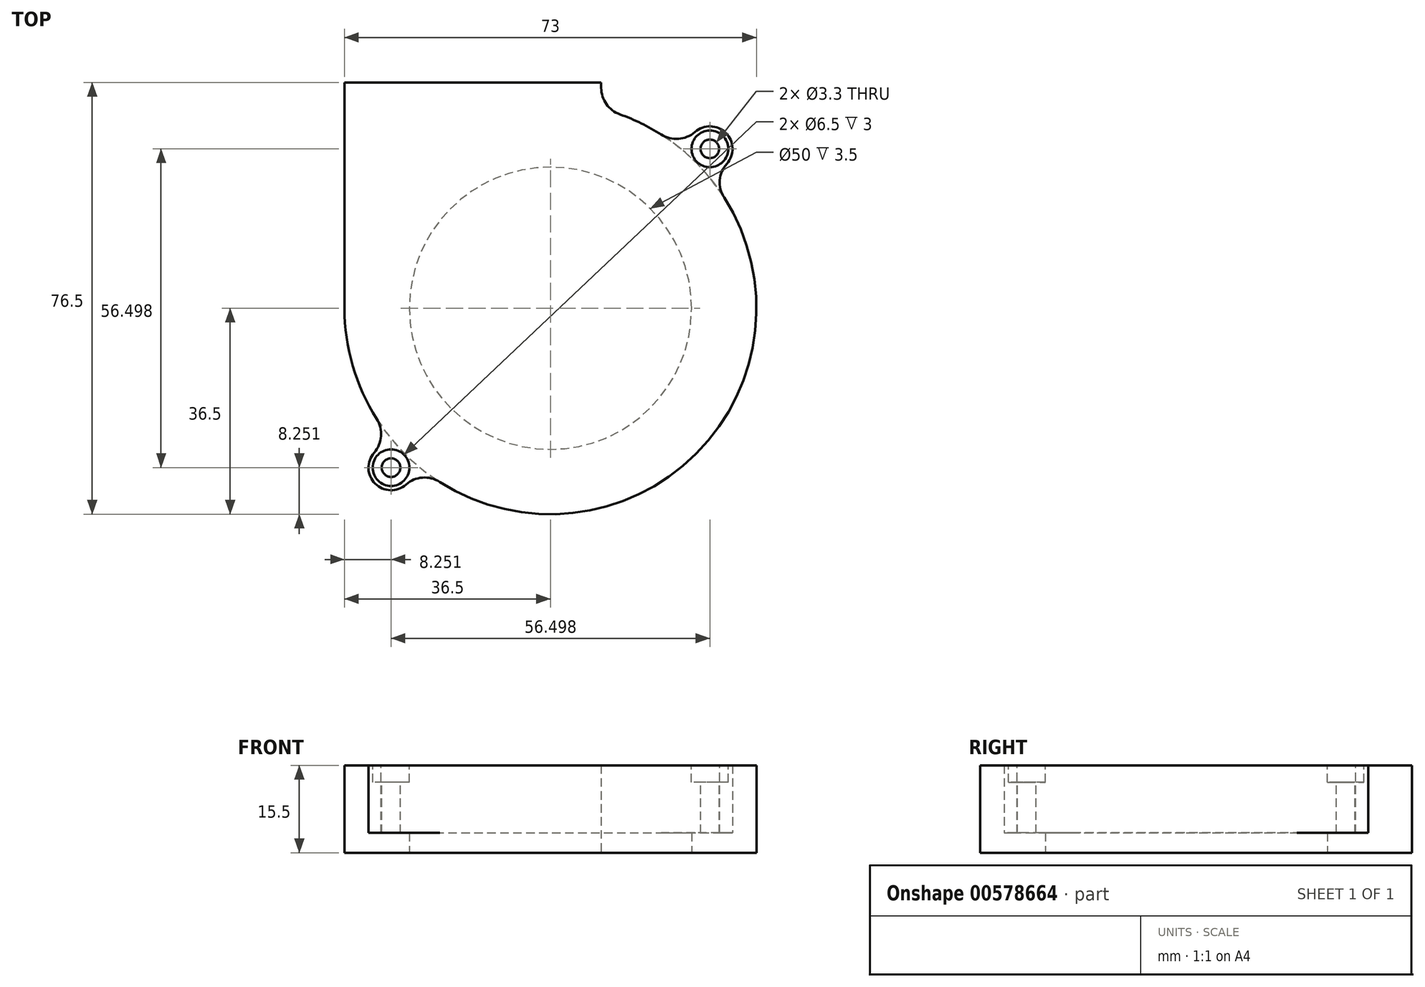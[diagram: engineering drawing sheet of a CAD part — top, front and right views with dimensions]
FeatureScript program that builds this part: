
annotation { "Feature Type Name" : "Feature", "Feature Type Description" : "" }
export const myFeature = defineFeature(function(context is Context, id is Id, definition is map)
    precondition{}
    {
        {
            var Q0;
            Q0=qCreatedBy(makeId("Top.planeOp"),FACE);
            var sketch = newSketch(context, id + "F0", { "sketchPlane" : qUnion([Q0])});
            skArc(sketch, "E0", {"start": v(24.4, 27.14) * mm, "mid": v(17.2, 32.2) * mm, "end": v(9, 35.37) * mm});
            skLineSegment(sketch, "E1", {"start": v(9, 40) * mm, "end": v(-36.5, 40) * mm});
            skLineSegment(sketch, "E2", {"start": v(-36.5, 40) * mm, "end": v(-36.5, 0) * mm});
            skLineSegment(sketch, "E3", {"start": v(9, 40) * mm, "end": v(9, 35.37) * mm});
            skArc(sketch, "E4", {"start": v(27.14, 24.4) * mm, "mid": v(31.08, 31.08) * mm, "end": v(24.4, 27.14) * mm});
            skArc(sketch, "E5", {"start": v(-27.14, -24.4) * mm, "mid": v(-31.08, -31.08) * mm, "end": v(-24.4, -27.14) * mm});
            skLineSegment(sketch, "E6", {"start": v(28.25, 28.25) * mm, "end": v(-28.25, -28.25) * mm, "construction": true});
            skArc(sketch, "E7.trimOffspring", {"start": v(-24.4, -27.14) * mm, "mid": v(25.8, -25.8) * mm, "end": v(27.14, 24.4) * mm});
            skArc(sketch, "E8.trimOffspring", {"start": v(-36.5, 0) * mm, "mid": v(-34.08, -13.07) * mm, "end": v(-27.14, -24.4) * mm});
            skSolve(sketch);
        }
        {
            var Q0;
            Q0 = qSketchRegion(id + "F0", true);
            extrude(context, id + "F1", {"entities" : qUnion([Q0]), "depth" : 15.5 * mm, "offsetDistance" : 25 * mm});
        }
        {
            var Q0;
            Q0=makeQuery(id+"F1.opExtrude","CAP_FACE",FACE,{"disambiguationData":[OSD([sQuery(id+"F0.wireOp",EDGE,"E0"),sQuery(id+"F0.wireOp",EDGE,"E1"),sQuery(id+"F0.wireOp",EDGE,"E2"),sQuery(id+"F0.wireOp",EDGE,"E3"),sQuery(id+"F0.wireOp",EDGE,"E4"),sQuery(id+"F0.wireOp",EDGE,"E5"),sQuery(id+"F0.wireOp",EDGE,"E7.trimOffspring"),sQuery(id+"F0.wireOp",EDGE,"E8.trimOffspring")])],"isStart":true});
            var sketch = newSketch(context, id + "F2", { "sketchPlane" : qUnion([Q0])});
            skArc(sketch, "E9", {"start": v(24.4, -27.14) * mm, "mid": v(25.8, -25.8) * mm, "end": v(27.14, -24.4) * mm});
            skArc(sketch, "E10.0", {"start": v(-27.14, 24.4) * mm, "mid": v(-31.08, 31.08) * mm, "end": v(-24.4, 27.14) * mm});
            skArc(sketch, "E11.0", {"start": v(27.14, -24.4) * mm, "mid": v(31.08, -31.08) * mm, "end": v(24.4, -27.14) * mm});
            skArc(sketch, "E12.trimOffspring", {"start": v(-24.4, 27.14) * mm, "mid": v(-25.8, 25.8) * mm, "end": v(-27.14, 24.4) * mm});
            skCircle(sketch, "E13", {"center": v(0, 0) * mm, "radius": 25 * mm});
            skSolve(sketch);
        }
        {
            var Q0;
            Q0=makeQuery(id+"F2.imprint","IMPRINT",FACE,{"disambiguationData":[TD([[makeQuery(id+"F2.imprint","IMPRINT",EDGE,{"derivedFrom":sQuery(id+"F2.wireOp",EDGE,"E10.0")}),-1.0]])]});
            var Q1;
            Q1=makeQuery(id+"F2.imprint","IMPRINT",FACE,{"disambiguationData":[TD([[makeQuery(id+"F2.imprint","IMPRINT",EDGE,{"derivedFrom":sQuery(id+"F2.wireOp",EDGE,"E9")}),-1.0]])]});
            var Q2;
            Q2=makeQuery(id+"F2.imprint","IMPRINT",FACE,{"disambiguationData":[TD([[makeQuery(id+"F2.imprint","IMPRINT",EDGE,{"derivedFrom":sQuery(id+"F2.wireOp",EDGE,"E13")}),1.0]])]});
            extrude(context, id + "F3", {"entities" : qUnion([Q0, Q1, Q2]), "operationType" : NewBodyOperationType.REMOVE, "oppositeDirection" : true, "depth" : 3.5 * mm, "offsetDistance" : 25 * mm});
        }
        {
            var Q0;
            Q0=makeQuery(id+"F1.opExtrude","CAP_FACE",FACE,{"disambiguationData":[OSD([sQuery(id+"F0.wireOp",EDGE,"E0"),sQuery(id+"F0.wireOp",EDGE,"E1"),sQuery(id+"F0.wireOp",EDGE,"E2"),sQuery(id+"F0.wireOp",EDGE,"E3"),sQuery(id+"F0.wireOp",EDGE,"E4"),sQuery(id+"F0.wireOp",EDGE,"E5"),sQuery(id+"F0.wireOp",EDGE,"E7.trimOffspring"),sQuery(id+"F0.wireOp",EDGE,"E8.trimOffspring")])],"isStart":false});
            var sketch = newSketch(context, id + "F4", { "sketchPlane" : qUnion([Q0])});
            skPoint(sketch, "E14", {"position": v(-28.25, -28.25) * mm});
            skPoint(sketch, "E15", {"position": v(28.25, 28.25) * mm});
            skSolve(sketch);
        }
        {
            var Q0;
            Q0=sQuery(id+"F4.wireOp",VERTEX,"E14");
            var Q1;
            Q1=sQuery(id+"F4.wireOp",VERTEX,"E15");
            var Q2;
            Q2=makeQuery(id+"F1.opExtrude","SWEPT_BODY",BODY,{"disambiguationData":[OSD([sQuery(id+"F0.wireOp",EDGE,"E0"),sQuery(id+"F0.wireOp",EDGE,"E1"),sQuery(id+"F0.wireOp",EDGE,"E2"),sQuery(id+"F0.wireOp",EDGE,"E3"),sQuery(id+"F0.wireOp",EDGE,"E4"),sQuery(id+"F0.wireOp",EDGE,"E5"),sQuery(id+"F0.wireOp",EDGE,"E7.trimOffspring"),sQuery(id+"F0.wireOp",EDGE,"E8.trimOffspring")])]});
            hole(context, id + "F5", {"style" : HoleStyle.C_BORE, "endStyle" : HoleEndStyle.THROUGH, "standardTappedOrClearance" : lookupTablePath({ "standard" : "ISO", "fit" : "Normal", "size" : "M3", "type" : "Clearance" }), "standardBlindInLast" : lookupTablePath({ "fit" : "Standard", "standard" : "ISO", "size" : "M3", "type" : "Clearance" }), "holeDiameter" : 3.3 * mm, "cBoreDiameter" : 6.5 * mm, "cBoreDepth" : 3 * mm, "isTappedThrough" : true, "tappedDepth" : 12 * mm, "tapClearance" : 3, "locations" : qUnion([Q0, Q1]), "scope" : qUnion([Q2])});
        }
        {
            var Q0;
            Q0=makeQuery(id+"F1.opExtrude","SWEPT_EDGE",EDGE,{"disambiguationData":[OSD([sQuery(id+"F0.wireOp",EDGE,"E5"),sQuery(id+"F0.wireOp",EDGE,"E8.trimOffspring")])]});
            var Q1;
            Q1=makeQuery(id+"F1.opExtrude","SWEPT_EDGE",EDGE,{"disambiguationData":[OSD([sQuery(id+"F0.wireOp",EDGE,"E5"),sQuery(id+"F0.wireOp",EDGE,"E7.trimOffspring")])]});
            var Q2;
            Q2=makeQuery(id+"F1.opExtrude","SWEPT_EDGE",EDGE,{"disambiguationData":[OSD([sQuery(id+"F0.wireOp",EDGE,"E4"),sQuery(id+"F0.wireOp",EDGE,"E7.trimOffspring")])]});
            var Q3;
            Q3=makeQuery(id+"F1.opExtrude","SWEPT_EDGE",EDGE,{"disambiguationData":[OSD([sQuery(id+"F0.wireOp",EDGE,"E0"),sQuery(id+"F0.wireOp",EDGE,"E4")])]});
            var Q4;
            Q4=makeQuery(id+"F1.opExtrude","SWEPT_EDGE",EDGE,{"disambiguationData":[OSD([sQuery(id+"F0.wireOp",EDGE,"E0"),sQuery(id+"F0.wireOp",EDGE,"E3")])]});
            fillet(context, id + "F6", {"entities" : qUnion([Q0, Q1, Q2, Q3, Q4]), "radius" : 5 * mm, "tangentPropagation" : true, "allowEdgeOverflow" : false});
        }
    });
